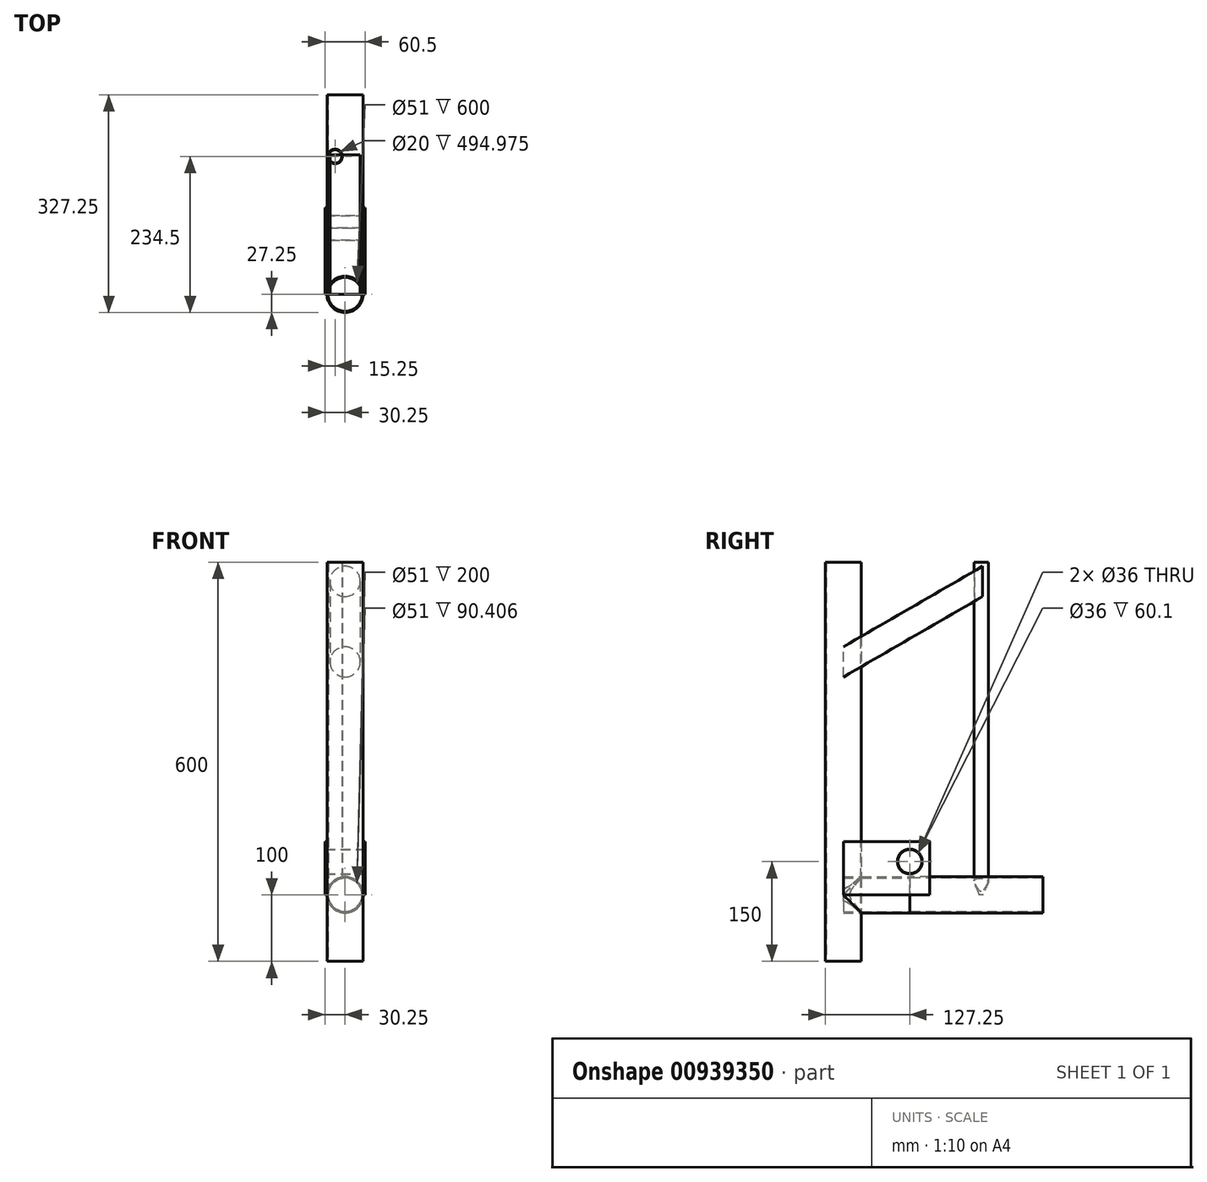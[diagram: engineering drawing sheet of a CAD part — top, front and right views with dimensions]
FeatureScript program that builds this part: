
annotation { "Feature Type Name" : "Feature", "Feature Type Description" : "" }
export const myFeature = defineFeature(function(context is Context, id is Id, definition is map)
    precondition{}
    {
        {
            var Q0;
            Q0=qCreatedBy(makeId("Top.planeOp"),FACE);
            var sketch = newSketch(context, id + "F0", { "sketchPlane" : qUnion([Q0])});
            skPoint(sketch, "E0", {"position": v(0, -100) * mm});
            skCircle(sketch, "E1", {"center": v(0, -100) * mm, "radius": 27.25 * mm});
            skPoint(sketch, "E2", {"position": v(0, 107.25) * mm});
            skCircle(sketch, "E3", {"center": v(-15, 107.25) * mm, "radius": 11 * mm});
            skCircle(sketch, "E4", {"center": v(-15, 107.25) * mm, "radius": 10 * mm});
            skCircle(sketch, "E5", {"center": v(0, -100) * mm, "radius": 25.5 * mm});
            skSolve(sketch);
        }
        {
            var Q0;
            Q0=makeQuery(id+"F0.imprint","IMPRINT",FACE,{"disambiguationData":[TD([[makeQuery(id+"F0.imprint","IMPRINT",EDGE,{"derivedFrom":sQuery(id+"F0.wireOp",EDGE,"E1")}),1.0]])]});
            var Q1;
            Q1=makeQuery(id+"F0.imprint","IMPRINT",FACE,{"disambiguationData":[TD([[makeQuery(id+"F0.imprint","IMPRINT",EDGE,{"derivedFrom":sQuery(id+"F0.wireOp",EDGE,"E3")}),1.0]])]});
            extrude(context, id + "F1", {"entities" : qUnion([Q0, Q1]), "depth" : 500 * mm, "offsetDistance" : 25 * mm});
        }
        {
            var Q0;
            Q0=makeQuery(id+"F1.opExtrude","CAP_FACE",FACE,{"disambiguationData":[OSD([sQuery(id+"F0.wireOp",EDGE,"E1"),sQuery(id+"F0.wireOp",EDGE,"E5")])],"isStart":true});
            extrude(context, id + "F2", {"entities" : qUnion([Q0]), "depth" : 100 * mm, "offsetDistance" : 25 * mm});
        }
        {
            var Q0;
            Q0=qCreatedBy(makeId("Front.planeOp"),FACE);
            var sketch = newSketch(context, id + "F3", { "sketchPlane" : qUnion([Q0])});
            skCircle(sketch, "E6", {"center": v(0, 0) * mm, "radius": 27.25 * mm});
            skCircle(sketch, "E7", {"center": v(0, 0) * mm, "radius": 25.5 * mm});
            skSolve(sketch);
        }
        {
            var Q0;
            Q0=makeQuery(id+"F3.imprint","IMPRINT",FACE,{"disambiguationData":[TD([[makeQuery(id+"F3.imprint","IMPRINT",EDGE,{"derivedFrom":sQuery(id+"F3.wireOp",EDGE,"E6")}),1.0]])]});
            extrude(context, id + "F4", {"entities" : qUnion([Q0]), "operationType" : NewBodyOperationType.ADD, "depth" : 100 * mm, "offsetDistance" : 25 * mm});
        }
        {
            var Q0;
            Q0=makeQuery(id+"F4.opExtrude","CAP_FACE",FACE,{"disambiguationData":[OSD([sQuery(id+"F3.wireOp",EDGE,"E6"),sQuery(id+"F3.wireOp",EDGE,"E7")])],"isStart":true});
            extrude(context, id + "F5", {"entities" : qUnion([Q0]), "depth" : 200 * mm, "offsetDistance" : 25 * mm});
        }
        {
            var Q0;
            Q0=makeQuery(id+"F3.imprint","IMPRINT",FACE,{"disambiguationData":[TD([[makeQuery(id+"F3.imprint","IMPRINT",EDGE,{"derivedFrom":sQuery(id+"F3.wireOp",EDGE,"E7")}),1.0]])]});
            extrude(context, id + "F6", {"entities" : qUnion([Q0]), "oppositeDirection" : true, "depth" : 200 * mm, "offsetDistance" : 25 * mm});
        }
        {
            var Q0;
            Q0=makeQuery(id+"F6.opExtrude","SWEPT_BODY",BODY,{"disambiguationData":[OSD([sQuery(id+"F3.wireOp",EDGE,"E7")])]});
            var Q1;
            Q1=makeQuery(id+"F1.opExtrude","SWEPT_BODY",BODY,{"disambiguationData":[OSD([sQuery(id+"F0.wireOp",EDGE,"E3"),sQuery(id+"F0.wireOp",EDGE,"E4")])]});
            booleanBodies(context, id + "F7", {"operationType" : BooleanOperationType.SUBTRACTION, "tools" : qUnion([Q0]), "targets" : qUnion([Q1])});
        }
        {
            var Q0;
            Q0=qCreatedBy(makeId("Right.planeOp"),FACE);
            cPlane(context, id + "F8", {"entities" : qUnion([Q0]), "cplaneType" : CPlaneType.OFFSET, "offset" : 27.25 * mm, "width" : 150 * mm, "height" : 150 * mm});
        }
        {
            var Q0;
            Q0=qCreatedBy(id+"F8.planeOp",FACE);
            var sketch = newSketch(context, id + "F9", { "sketchPlane" : qUnion([Q0])});
            skPoint(sketch, "E8", {"position": v(-100, 0) * mm});
            skLineSegment(sketch, "E9.bottom", {"start": v(-100, 0) * mm, "end": v(30, 0) * mm});
            skLineSegment(sketch, "E9.top", {"start": v(-100, 80) * mm, "end": v(30, 80) * mm});
            skLineSegment(sketch, "E9.left", {"start": v(-100, 0) * mm, "end": v(-100, 80) * mm});
            skLineSegment(sketch, "E9.right", {"start": v(30, 0) * mm, "end": v(30, 80) * mm});
            skSolve(sketch);
        }
        {
            var Q0;
            Q0=makeQuery(id+"F9.imprint","IMPRINT",FACE,{"disambiguationData":[TD([[makeQuery(id+"F9.imprint","IMPRINT",EDGE,{"derivedFrom":sQuery(id+"F9.wireOp",EDGE,"E9.bottom")}),1.0]])]});
            extrude(context, id + "F10", {"entities" : qUnion([Q0]), "depth" : 3 * mm, "offsetDistance" : 25 * mm});
        }
        {
            var Q0;
            Q0=makeQuery(id+"F10.opExtrude","SWEPT_BODY",BODY,{"disambiguationData":[OSD([sQuery(id+"F9.wireOp",EDGE,"E9.bottom"),sQuery(id+"F9.wireOp",EDGE,"E9.top"),sQuery(id+"F9.wireOp",EDGE,"E9.left"),sQuery(id+"F9.wireOp",EDGE,"E9.right")])]});
            var Q1;
            Q1=qCreatedBy(makeId("Right.planeOp"),FACE);
            mirror(context, id + "F11", {"entities" : qUnion([Q0]), "mirrorPlane" : qUnion([Q1])});
        }
        {
            var Q0;
            Q0=makeQuery(id+"F10.opExtrude","CAP_FACE",FACE,{"disambiguationData":[OSD([sQuery(id+"F9.wireOp",EDGE,"E9.bottom"),sQuery(id+"F9.wireOp",EDGE,"E9.top"),sQuery(id+"F9.wireOp",EDGE,"E9.left"),sQuery(id+"F9.wireOp",EDGE,"E9.right")])],"isStart":false});
            var sketch = newSketch(context, id + "F12", { "sketchPlane" : qUnion([Q0])});
            skPoint(sketch, "E10", {"position": v(0, 50) * mm});
            skCircle(sketch, "E11", {"center": v(0, 50) * mm, "radius": 18.73 * mm});
            skCircle(sketch, "E12", {"center": v(0, 50) * mm, "radius": 18 * mm});
            skSolve(sketch);
        }
        {
            var Q0;
            Q0=makeQuery(id+"F12.imprint","IMPRINT",FACE,{"disambiguationData":[TD([[makeQuery(id+"F12.imprint","IMPRINT",EDGE,{"derivedFrom":sQuery(id+"F12.wireOp",EDGE,"E11")}),1.0]])]});
            extrude(context, id + "F13", {"entities" : qUnion([Q0]), "oppositeDirection" : true, "depth" : 60.1 * mm, "offsetDistance" : 25 * mm});
        }
        {
            var Q0;
            Q0=makeQuery(id+"F12.imprint","IMPRINT",FACE,{"disambiguationData":[TD([[makeQuery(id+"F12.imprint","IMPRINT",EDGE,{"derivedFrom":sQuery(id+"F12.wireOp",EDGE,"E12")}),1.0]])]});
            extrude(context, id + "F14", {"entities" : qUnion([Q0]), "endBound" : BoundingType.SYMMETRIC, "oppositeDirection" : true, "depth" : 176 * mm, "offsetDistance" : 25 * mm});
        }
        {
            var Q0;
            Q0=makeQuery(id+"F14.opExtrude","SWEPT_BODY",BODY,{"disambiguationData":[OSD([sQuery(id+"F12.wireOp",EDGE,"E12")])]});
            var Q1;
            Q1=makeQuery(id+"F10.opExtrude","SWEPT_BODY",BODY,{"disambiguationData":[OSD([sQuery(id+"F9.wireOp",EDGE,"E9.bottom"),sQuery(id+"F9.wireOp",EDGE,"E9.top"),sQuery(id+"F9.wireOp",EDGE,"E9.left"),sQuery(id+"F9.wireOp",EDGE,"E9.right")])]});
            var Q2;
            Q2=makeQuery(id+"F11.opPattern","COPY",BODY,{"derivedFrom":makeQuery(id+"F10.opExtrude","SWEPT_BODY",BODY,{"disambiguationData":[OSD([sQuery(id+"F9.wireOp",EDGE,"E9.bottom"),sQuery(id+"F9.wireOp",EDGE,"E9.top"),sQuery(id+"F9.wireOp",EDGE,"E9.left"),sQuery(id+"F9.wireOp",EDGE,"E9.right")])]}),"instanceName":"1"});
            var Q3;
            Q3=makeQuery(id+"F13.opExtrude","SWEPT_BODY",BODY,{"disambiguationData":[OSD([sQuery(id+"F12.wireOp",EDGE,"E11"),sQuery(id+"F12.wireOp",EDGE,"E12")])]});
            booleanBodies(context, id + "F15", {"operationType" : BooleanOperationType.SUBTRACTION, "tools" : qUnion([Q0]), "targets" : qUnion([Q1, Q2, Q3])});
        }
        {
            var Q0;
            Q0=qCreatedBy(makeId("Right.planeOp"),FACE);
            var sketch = newSketch(context, id + "F16", { "sketchPlane" : qUnion([Q0])});
            skPoint(sketch, "E13", {"position": v(-100, 350) * mm});
            skLineSegment(sketch, "E14", {"start": v(-100, 350) * mm, "end": v(109.5, 470.95) * mm});
            skSolve(sketch);
        }
        {
            var Q0;
            Q0=qCreatedBy(makeId("Front.planeOp"),FACE);
            cPlane(context, id + "F17", {"entities" : qUnion([Q0]), "cplaneType" : CPlaneType.OFFSET, "offset" : 100 * mm, "width" : 150 * mm, "height" : 150 * mm});
        }
        {
            var Q0;
            Q0=qCreatedBy(id+"F17.planeOp",FACE);
            var sketch = newSketch(context, id + "F18", { "sketchPlane" : qUnion([Q0])});
            skPoint(sketch, "E15", {"position": v(0, 350) * mm});
            skCircle(sketch, "E16", {"center": v(0, 350) * mm, "radius": 22.75 * mm});
            skSolve(sketch);
        }
        {
            var Q0;
            Q0 = qSketchRegion(id + "F18", true);
            var Q1;
            Q1=sQuery(id+"F16.wireOp",EDGE,"E14");
            sweep(context, id + "F19", {"profiles" : qUnion([Q0]), "path" : qUnion([Q1])});
        }
    });
